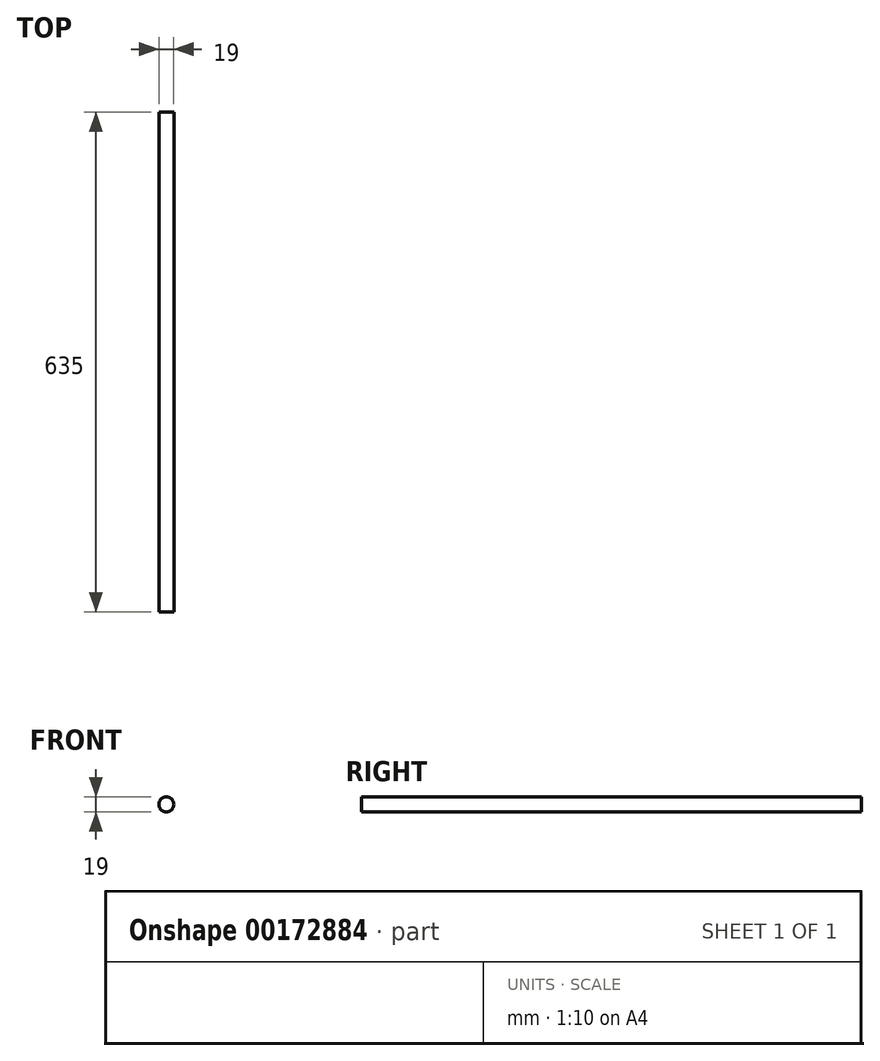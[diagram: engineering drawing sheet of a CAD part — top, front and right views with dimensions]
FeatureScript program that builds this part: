
annotation { "Feature Type Name" : "Feature", "Feature Type Description" : "" }
export const myFeature = defineFeature(function(context is Context, id is Id, definition is map)
    precondition{}
    {
        {
            var Q0;
            Q0=qCreatedBy(makeId("Front.planeOp"),FACE);
            var sketch = newSketch(context, id + "F0", { "sketchPlane" : qUnion([Q0])});
            skCircle(sketch, "E0", {"center": v(0, 0) * mm, "radius": 9.5 * mm});
            skSolve(sketch);
        }
        {
            var Q0;
            Q0=sQuery(id+"F0.wireOp",EDGE,"E0");
            extrude(context, id + "F1", {"bodyType" : ToolBodyType.SURFACE, "surfaceEntities" : qUnion([Q0]), "depth" : 635 * mm});
        }
    });
